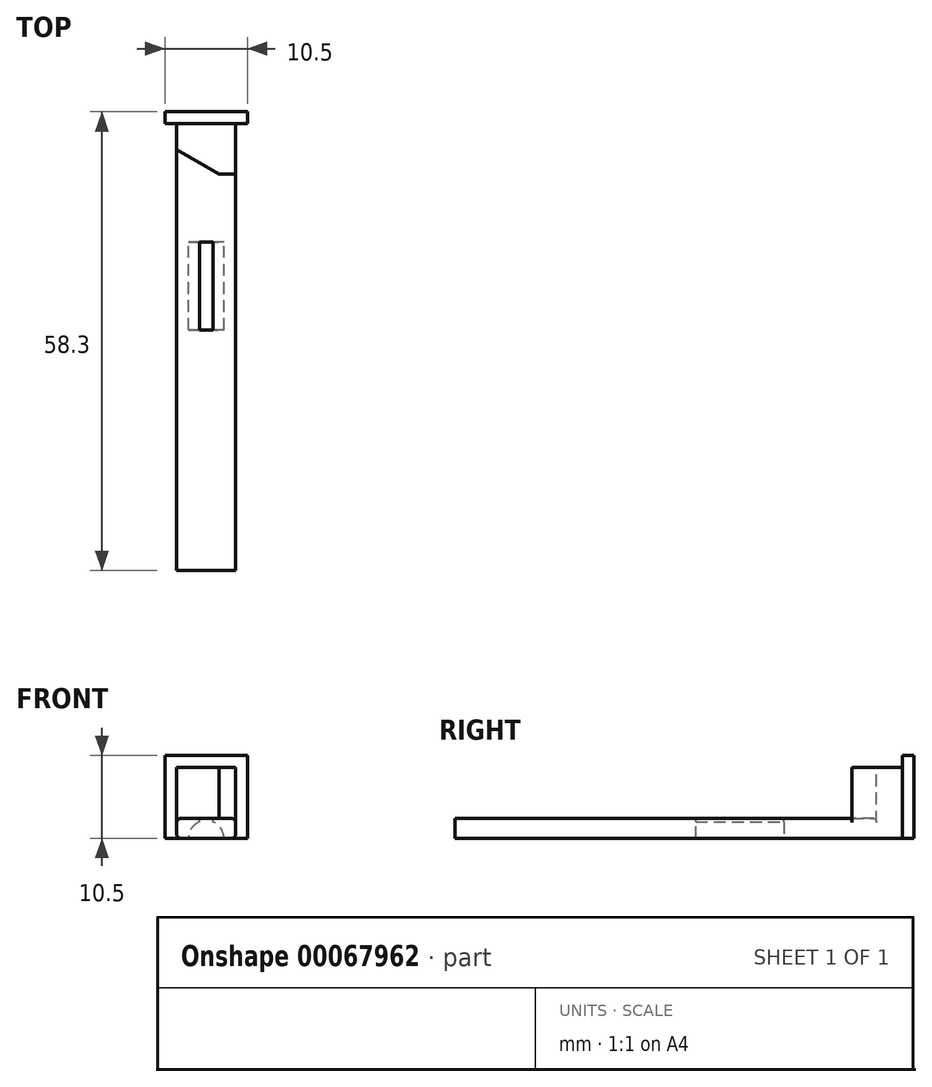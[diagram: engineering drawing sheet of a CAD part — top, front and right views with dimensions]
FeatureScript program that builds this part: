
annotation { "Feature Type Name" : "Feature", "Feature Type Description" : "" }
export const myFeature = defineFeature(function(context is Context, id is Id, definition is map)
    precondition{}
    {
        {
            var Q0;
            Q0=qCreatedBy(makeId("Right.planeOp"),FACE);
            var sketch = newSketch(context, id + "F0", { "sketchPlane" : qUnion([Q0])});
            skLineSegment(sketch, "E0.rect.bottom", {"start": v(15.24, 2.5) * mm, "end": v(-37.56, 2.5) * mm});
            skLineSegment(sketch, "E0.rect.top", {"start": v(15.24, 0) * mm, "end": v(-37.56, 0) * mm});
            skLineSegment(sketch, "E0.rect.left", {"start": v(15.24, 2.5) * mm, "end": v(15.24, 0) * mm});
            skLineSegment(sketch, "E0.rect.right", {"start": v(-37.56, 2.5) * mm, "end": v(-37.56, 0) * mm});
            skLineSegment(sketch, "E1.bottom", {"start": v(15.24, 2.5) * mm, "end": v(8.84, 2.5) * mm});
            skLineSegment(sketch, "E1.top", {"start": v(15.24, 9) * mm, "end": v(8.84, 9) * mm});
            skLineSegment(sketch, "E1.left", {"start": v(15.24, 2.5) * mm, "end": v(15.24, 9) * mm});
            skLineSegment(sketch, "E1.right", {"start": v(8.84, 2.5) * mm, "end": v(8.84, 9) * mm});
            skLineSegment(sketch, "E2.bottom", {"start": v(-37.56, 0) * mm, "end": v(-41.56, 0) * mm});
            skLineSegment(sketch, "E2.top", {"start": v(-37.56, 2.5) * mm, "end": v(-41.56, 2.5) * mm});
            skLineSegment(sketch, "E2.left", {"start": v(-37.56, 0) * mm, "end": v(-37.56, 2.5) * mm});
            skLineSegment(sketch, "E2.right", {"start": v(-41.56, 0) * mm, "end": v(-41.56, 2.5) * mm});
            skSolve(sketch);
        }
        {
            var Q0;
            Q0 = qSketchRegion(id + "F0", true);
            extrude(context, id + "F1", {"entities" : qUnion([Q0]), "endBound" : BoundingType.SYMMETRIC, "depth" : 7.5 * mm});
        }
        {
            var Q0;
            Q0=makeQuery(id+"F1.opExtrude","CAP_EDGE",EDGE,{"disambiguationData":[OSD([sQuery(id+"F0.wireOp",EDGE,"E1.right")])],"isStart":true});
            chamfer(context, id + "F2", {"entities" : qUnion([Q0]), "chamferType" : ChamferType.OFFSET_ANGLE, "width" : 3.1 * mm, "oppositeDirection" : false, "angle" : 60 * degree});
        }
        {
            var Q0;
            Q0=makeQuery(id+"F1.opExtrude","SWEPT_FACE",FACE,{"disambiguationData":[OSD([sQuery(id+"F0.wireOp",EDGE,"E0.rect.left"),sQuery(id+"F0.wireOp",EDGE,"E1.left")])]});
            var sketch = newSketch(context, id + "F3", { "sketchPlane" : qUnion([Q0])});
            skLineSegment(sketch, "E3.0.0", {"start": v(3.75, 0) * mm, "end": v(3.75, 9) * mm, "construction": true});
            skLineSegment(sketch, "E3.0.1", {"start": v(3.75, 9) * mm, "end": v(-3.75, 9) * mm, "construction": true});
            skLineSegment(sketch, "E3.0.2", {"start": v(-3.75, 9) * mm, "end": v(-3.75, 0) * mm, "construction": true});
            skLineSegment(sketch, "E3.0.3", {"start": v(-3.75, 0) * mm, "end": v(3.75, 0) * mm, "construction": true});
            skLineSegment(sketch, "E4.bottom", {"start": v(-5.25, 0) * mm, "end": v(5.25, 0) * mm});
            skLineSegment(sketch, "E4.top", {"start": v(-5.25, 10.5) * mm, "end": v(5.25, 10.5) * mm});
            skLineSegment(sketch, "E4.left", {"start": v(-5.25, 0) * mm, "end": v(-5.25, 10.5) * mm});
            skLineSegment(sketch, "E4.right", {"start": v(5.25, 0) * mm, "end": v(5.25, 10.5) * mm});
            skSolve(sketch);
        }
        {
            var Q0;
            Q0 = qSketchRegion(id + "F3", true);
            extrude(context, id + "F4", {"entities" : qUnion([Q0]), "operationType" : NewBodyOperationType.ADD, "depth" : 1.5 * mm});
        }
        {
            var Q0;
            Q0=qCreatedBy(makeId("Front.planeOp"),FACE);
            var sketch = newSketch(context, id + "F5", { "sketchPlane" : qUnion([Q0])});
            skArc(sketch, "E5", {"start": v(-2.25, 0) * mm, "mid": v(0, 2.25) * mm, "end": v(2.25, 0) * mm});
            skLineSegment(sketch, "E6", {"start": v(-2.25, 0) * mm, "end": v(2.25, 0) * mm});
            skLineSegment(sketch, "E7.bottom", {"start": v(-0.86, 0) * mm, "end": v(0.86, 0) * mm, "construction": true});
            skLineSegment(sketch, "E7.top", {"start": v(-0.86, 4.63) * mm, "end": v(0.86, 4.63) * mm});
            skLineSegment(sketch, "E7.left", {"start": v(-0.86, 0) * mm, "end": v(-0.86, 4.63) * mm});
            skLineSegment(sketch, "E7.right", {"start": v(0.86, 0) * mm, "end": v(0.86, 4.63) * mm});
            skLineSegment(sketch, "E8", {"start": v(0, 0) * mm, "end": v(-0.86, 2.08) * mm, "construction": true});
            skLineSegment(sketch, "E9", {"start": v(0, 0) * mm, "end": v(0.86, 2.08) * mm, "construction": true});
            skSolve(sketch);
        }
        {
            var Q0;
            Q0 = qSketchRegion(id + "F5", true);
            extrude(context, id + "F6", {"entities" : qUnion([Q0]), "operationType" : NewBodyOperationType.REMOVE, "depth" : 11 * mm, "hasSecondDirection" : true, "secondDirectionOppositeDirection" : true, "secondDirectionDepth" : 0.2 * mm});
        }
        {
            var Q0;
            Q0=makeQuery(id+"F1.opExtrude","CAP_EDGE",EDGE,{"disambiguationData":[OSD([sQuery(id+"F0.wireOp",EDGE,"E0.rect.top"),sQuery(id+"F0.wireOp",EDGE,"E2.bottom")])],"isStart":true});
            var Q1;
            Q1=makeQuery(id+"F1.opExtrude","CAP_EDGE",EDGE,{"disambiguationData":[OSD([sQuery(id+"F0.wireOp",EDGE,"E0.rect.bottom"),sQuery(id+"F0.wireOp",EDGE,"E2.top")])],"isStart":true});
            var Q2;
            Q2=makeQuery(id+"F1.opExtrude","CAP_EDGE",EDGE,{"disambiguationData":[OSD([sQuery(id+"F0.wireOp",EDGE,"E0.rect.bottom"),sQuery(id+"F0.wireOp",EDGE,"E2.top")])],"isStart":false});
            var Q3;
            Q3=makeQuery(id+"F1.opExtrude","CAP_EDGE",EDGE,{"disambiguationData":[OSD([sQuery(id+"F0.wireOp",EDGE,"E0.rect.top"),sQuery(id+"F0.wireOp",EDGE,"E2.bottom")])],"isStart":false});
            fillet(context, id + "F7", {"entities" : qUnion([Q0, Q1, Q2, Q3]), "radius" : 0.5 * mm, "allowEdgeOverflow" : false});
        }
    });
